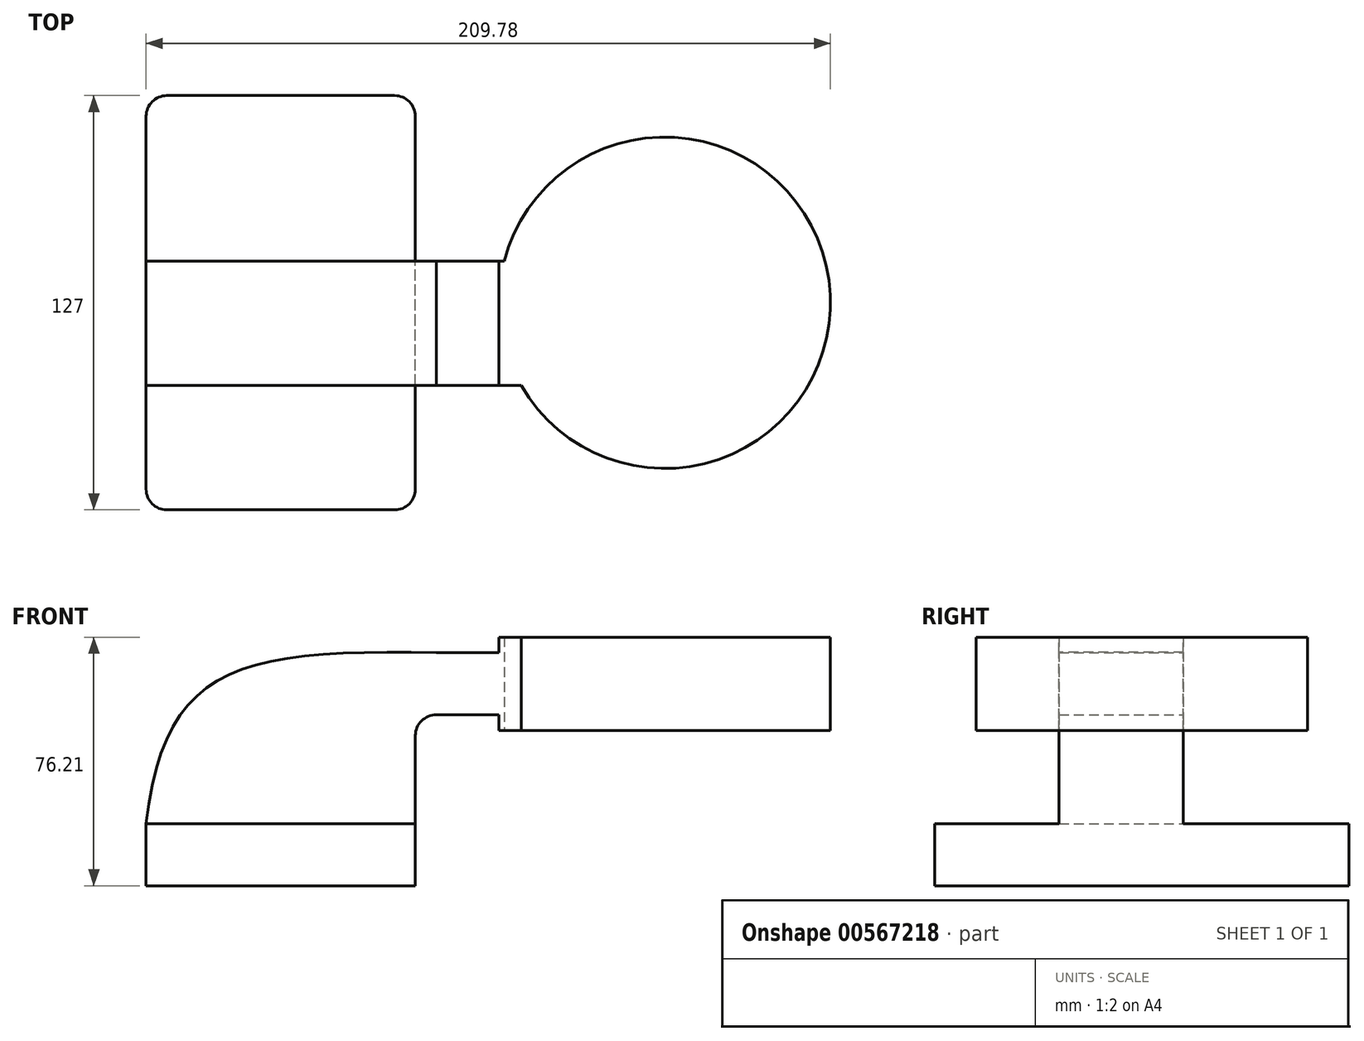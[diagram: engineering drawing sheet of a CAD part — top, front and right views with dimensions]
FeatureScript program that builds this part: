
annotation { "Feature Type Name" : "Feature", "Feature Type Description" : "" }
export const myFeature = defineFeature(function(context is Context, id is Id, definition is map)
    precondition{}
    {
        {
            var Q0;
            Q0=qCreatedBy(makeId("Front.planeOp"),FACE);
            var sketch = newSketch(context, id + "F0", { "sketchPlane" : qUnion([Q0])});
            skLineSegment(sketch, "E0.bottom", {"start": v(-41.28, 9.52) * mm, "end": v(41.28, 9.53) * mm});
            skLineSegment(sketch, "E0.top", {"start": v(-41.28, -9.53) * mm, "end": v(41.28, -9.52) * mm});
            skLineSegment(sketch, "E0.left", {"start": v(-41.28, 9.52) * mm, "end": v(-41.28, -9.53) * mm});
            skLineSegment(sketch, "E0.right", {"start": v(41.28, 9.53) * mm, "end": v(41.28, -9.52) * mm});
            skPoint(sketch, "E0.middle", {"position": v(0, 0) * mm});
            skLineSegment(sketch, "E1.bottom", {"start": v(66.9, 38.1) * mm, "end": v(117.7, 38.1) * mm});
            skLineSegment(sketch, "E1.top", {"start": v(66.9, 66.68) * mm, "end": v(117.7, 66.68) * mm});
            skLineSegment(sketch, "E1.left", {"start": v(66.9, 38.1) * mm, "end": v(66.9, 66.68) * mm});
            skLineSegment(sketch, "E1.right", {"start": v(117.7, 38.1) * mm, "end": v(117.7, 66.68) * mm});
            skPoint(sketch, "E1.middle", {"position": v(92.3, 52.38) * mm});
            skLineSegment(sketch, "E2", {"start": v(41.28, 9.53) * mm, "end": v(41.28, 36.47) * mm});
            skArc(sketch, "E3", {"start": v(41.28, 36.47) * mm, "mid": v(43.15, 41) * mm, "end": v(47.68, 42.88) * mm});
            skLineSegment(sketch, "E4", {"start": v(47.68, 42.88) * mm, "end": v(85.14, 42.88) * mm});
            skLineSegment(sketch, "E5.0", {"start": v(47.68, 61.93) * mm, "end": v(85.14, 61.93) * mm});
            skArc(sketch, "E5.1", {"start": v(22.23, 36.47) * mm, "mid": v(29.68, 54.47) * mm, "end": v(47.68, 61.93) * mm});
            skLineSegment(sketch, "E5.2", {"start": v(22.23, 9.53) * mm, "end": v(22.23, 36.47) * mm});
            skFitSpline(sketch, "E6", {"points": [v(-41.28, 9.52) * mm, v(47.68, 61.93) * mm], "startDerivative": vector(17.13, 144.81) * mm, "endDerivative": vector(184.08, -3.53) * mm});
            skSolve(sketch);
        }
        {
            var Q0;
            Q0 = qSketchRegion(id + "F0", true);
            extrude(context, id + "F1", {"entities" : qUnion([Q0]), "endBound" : BoundingType.SYMMETRIC, "depth" : 25.4 * mm, "offsetDistance" : 25.4 * mm});
        }
        {
            var Q0;
            Q0=makeQuery(id+"F0.imprint","IMPRINT",FACE,{"disambiguationData":[TD([[makeQuery(id+"F0.imprint","IMPRINT",EDGE,{"derivedFrom":sQuery(id+"F0.wireOp",EDGE,"E0.top")}),1.0]])]});
            extrude(context, id + "F2", {"entities" : qUnion([Q0]), "operationType" : NewBodyOperationType.ADD, "endBound" : BoundingType.SYMMETRIC, "depth" : 127 * mm, "offsetDistance" : 25.4 * mm});
        }
        {
            var Q0;
            Q0 = qSketchRegion(id + "F0", true);
            extrude(context, id + "F3", {"entities" : qUnion([Q0]), "operationType" : NewBodyOperationType.ADD, "depth" : 25.4 * mm, "offsetDistance" : 25.4 * mm});
        }
        {
            var Q0;
            {var subQ3=sQuery(id+"F0.wireOp",EDGE,"E1.bottom");Q0=makeQuery(id+"F0.imprint","IMPRINT",FACE,{"disambiguationData":[TD([[makeQuery(id+"F0.imprint","IMPRINT",EDGE,{"derivedFrom":subQ3}),1.0]])]});}
            var Q1;
            Q1=sQuery(id+"F0.wireOp",EDGE,"E1.right");
            revolve(context, id + "F4", {"operationType" : NewBodyOperationType.ADD, "entities" : qUnion([Q0]), "axis" : qUnion([Q1]), "revolveType" : RevolveType.FULL});
        }
        {
            var Q0;
            Q0=makeQuery(id+"F2.opExtrude","CAP_EDGE",EDGE,{"disambiguationData":[OSD([sQuery(id+"F0.wireOp",EDGE,"E0.left")])],"isStart":false});
            var Q1;
            Q1=makeQuery(id+"F2.opExtrude","CAP_EDGE",EDGE,{"disambiguationData":[OSD([sQuery(id+"F0.wireOp",EDGE,"E0.right")])],"isStart":false});
            var Q2;
            Q2=makeQuery(id+"F2.opExtrude","CAP_EDGE",EDGE,{"disambiguationData":[OSD([sQuery(id+"F0.wireOp",EDGE,"E0.left")])],"isStart":true});
            var Q3;
            Q3=makeQuery(id+"F2.opExtrude","CAP_EDGE",EDGE,{"disambiguationData":[OSD([sQuery(id+"F0.wireOp",EDGE,"E0.right")])],"isStart":true});
            fillet(context, id + "F5", {"entities" : qUnion([Q0, Q1, Q2, Q3]), "radius" : 6.35 * mm, "tangentPropagation" : true, "allowEdgeOverflow" : false});
        }
    });
